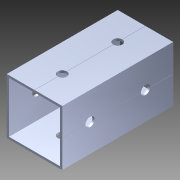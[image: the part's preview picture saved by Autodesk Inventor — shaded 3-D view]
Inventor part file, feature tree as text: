
AUTODESK INVENTOR PART (.ipt)
format: ipt  version: 2014 (Build 180170000, 170)  size: 1,162,240 bytes
history: native  units: in
note: dims shown in document units (in); Inventor stores cm internally (conversion verified against a paired STEP export)
features: pattern_circular x1, other x1, plane x1, extrude x1, imported_body x1, sketch x1
ambient origin geometry x8: Origin, YZ Plane, XZ Plane, XY Plane, X Axis, Y Axis, Z Axis, Center Point
bodies: Body1 (feature_tree)
feature tree (6):
  pattern_circular  "CirPattern2"
  other  "217-3426-STEP1"
  plane  "Work Plane1"
  extrude  "Extrusion1"  Depth=3937.0079in TaperAngle=0.0deg
  imported_body  "Base1"
  sketch  "Sketch1"  dims[d0=-2.0in d1=3937.0079in d2=0.0in]
